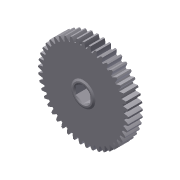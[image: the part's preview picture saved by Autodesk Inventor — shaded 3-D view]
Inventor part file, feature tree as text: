
AUTODESK INVENTOR PART (.ipt)
format: ipt  version: 2013 (Build 170138000, 138)  size: 374,272 bytes
history: native  units: mm (DEFAULTED — no unit token found)
features: sketch x5, extrude x3, plane x3, other x3, revolve x1, projected_geometry x1
ambient origin geometry x8: Origin, YZ Plane, XZ Plane, XY Plane, X Axis, Y Axis, Z Axis, Center Point
bodies: Solid1 (feature_tree)
feature tree (16):
  extrude  "Extrusion1"  Depth=9.525mm TaperAngle=0.0deg
  plane  "Work Plane1"
  plane  "Work Plane2"
  plane  "Work Plane3"
  other  "Spur Gear"
  extrude  "Extrusion2"  Depth=76.2mm TaperAngle=0.0deg
  extrude  "Extrusion3"  Depth=15.9004mm
  revolve  "Revolution1"  [1 undecoded]
  sketch  "Sketch1"  dims[d0=59.69mm d1=9.525mm d2=0.0mm]
  sketch  "Sketch2"  dims[d3=57.15mm d4=76.2mm d5=0.0mm]
  other  "Srf1"
  sketch  "Sketch3"  dims[d6=0.0mm d7=0.698132mm d20=15.9004mm]
  sketch  "Sketch4"  dims[d21=0.635mm d22=0.0mm d23=9.525mm]
  sketch  "Sketch5"  dims[d24=0.635mm d25=0.0mm d26=1.143mm d27=0.889mm d28=5.070181mm d29=2.54mm d30=90.0deg]
  other  "Pitch Diameter"
  projected_geometry  "Project Cut Edges1"
note: 1 required parameter value undecoded (feature->parameter linkage not recoverable at this tier; creation-order binding heuristic only, values carry confidence <= 0.55)
